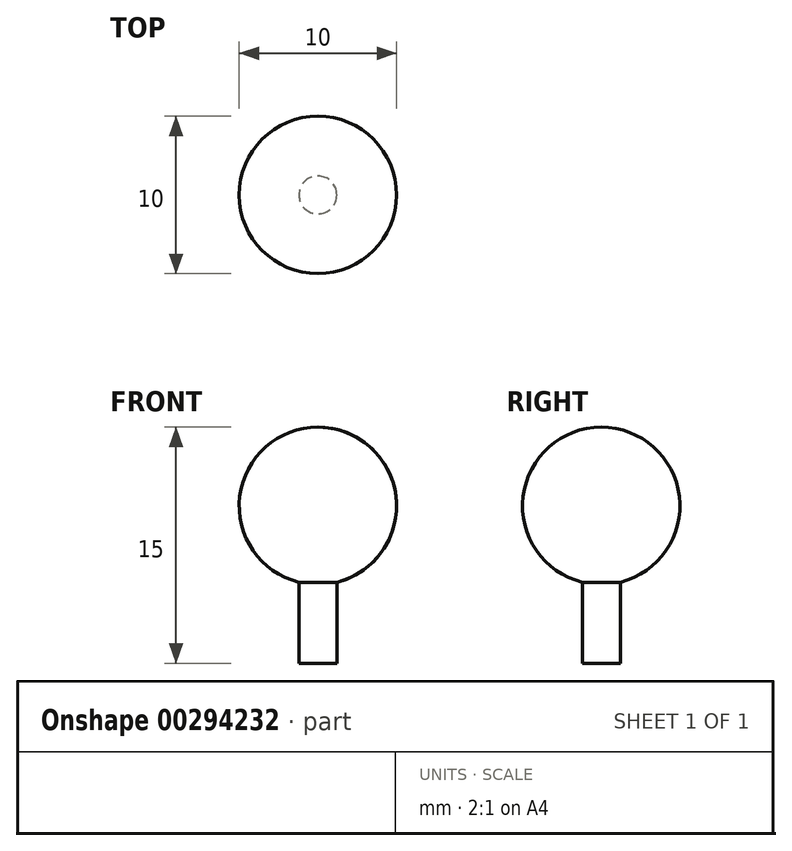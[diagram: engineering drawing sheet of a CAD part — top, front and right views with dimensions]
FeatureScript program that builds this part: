
annotation { "Feature Type Name" : "Feature", "Feature Type Description" : "" }
export const myFeature = defineFeature(function(context is Context, id is Id, definition is map)
    precondition{}
    {
        {
            var Q0;
            Q0=qCreatedBy(makeId("Front.planeOp"),FACE);
            var sketch = newSketch(context, id + "F0", { "sketchPlane" : qUnion([Q0])});
            skArc(sketch, "E0", {"start": v(1.2, -4.85) * mm, "mid": v(4.96, 0.6) * mm, "end": v(0, 5) * mm});
            skLineSegment(sketch, "E1.top", {"start": v(0, -10) * mm, "end": v(1.2, -10) * mm});
            skLineSegment(sketch, "E1.right", {"start": v(1.2, -4.85) * mm, "end": v(1.2, -10) * mm});
            skPoint(sketch, "E2.orphan", {"position": v(-1.2, 10) * mm});
            skPoint(sketch, "E3.orphan", {"position": v(1.2, 10) * mm});
            skLineSegment(sketch, "E4", {"start": v(0, 5) * mm, "end": v(0, -10) * mm});
            skPoint(sketch, "E5.orphan", {"position": v(-1.2, -10) * mm});
            skLineSegment(sketch, "E6", {"start": v(0, 10.27) * mm, "end": v(0, -15.35) * mm, "construction": true});
            skSolve(sketch);
        }
        {
            var Q0;
            Q0 = qSketchRegion(id + "F0", true);
            var Q1;
            Q1=sQuery(id+"F0.wireOp",EDGE,"E4");
            revolve(context, id + "F1", {"entities" : qUnion([Q0]), "axis" : qUnion([Q1]), "revolveType" : RevolveType.FULL});
        }
    });
